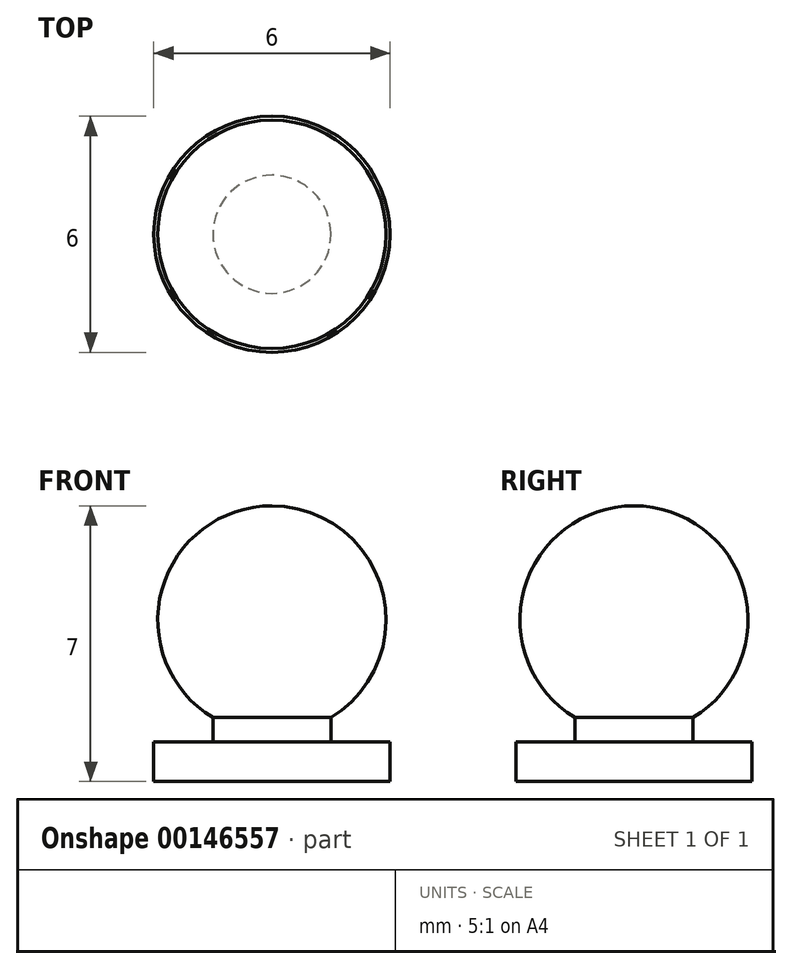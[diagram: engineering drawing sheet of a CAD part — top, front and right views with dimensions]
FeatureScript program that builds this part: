
annotation { "Feature Type Name" : "Feature", "Feature Type Description" : "" }
export const myFeature = defineFeature(function(context is Context, id is Id, definition is map)
    precondition{}
    {
        {
            var Q0;
            Q0=qCreatedBy(makeId("Front.planeOp"),FACE);
            var sketch = newSketch(context, id + "F0", { "sketchPlane" : qUnion([Q0])});
            skLineSegment(sketch, "E0", {"start": v(0, 39.67) * mm, "end": v(0, -40.6) * mm, "construction": true});
            skSolve(sketch);
        }
        {
            var Q0;
            Q0=qCreatedBy(makeId("Front.planeOp"),FACE);
            var sketch = newSketch(context, id + "F1", { "sketchPlane" : qUnion([Q0])});
            skLineSegment(sketch, "E1", {"start": v(-3, 0) * mm, "end": v(-3, 1) * mm});
            skLineSegment(sketch, "E2", {"start": v(-3, 1) * mm, "end": v(-1.5, 1) * mm});
            skLineSegment(sketch, "E3", {"start": v(-1.5, 1) * mm, "end": v(-1.5, 1.62) * mm});
            skArc(sketch, "E4", {"start": v(0, 7) * mm, "mid": v(-2.8, 4.88) * mm, "end": v(-1.5, 1.62) * mm});
            skLineSegment(sketch, "E5", {"start": v(-3, 0) * mm, "end": v(0, 0) * mm});
            skLineSegment(sketch, "E6", {"start": v(0, 0) * mm, "end": v(0, 7) * mm});
            skSolve(sketch);
        }
        {
            var Q0;
            Q0 = qSketchRegion(id + "F1", true);
            var Q1;
            Q1=sQuery(id+"F0.wireOp",EDGE,"E0");
            revolve(context, id + "F2", {"entities" : qUnion([Q0]), "axis" : qUnion([Q1]), "revolveType" : RevolveType.FULL});
        }
    });
